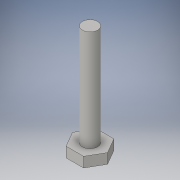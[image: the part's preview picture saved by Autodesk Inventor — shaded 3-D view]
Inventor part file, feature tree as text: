
AUTODESK INVENTOR PART (.ipt)
format: ipt  version: 2016 (Build 200138000, 138)  size: 100,864 bytes
history: native  units: in
note: dims shown in document units (in); Inventor stores cm internally (conversion verified against a paired STEP export)
features: sketch x3, extrude x2
ambient origin geometry x8: Origin, YZ Plane, XZ Plane, XY Plane, X Axis, Y Axis, Z Axis, Center Point
bodies: Solid1 (feature_tree)
feature tree (5):
  extrude  "Extrusion1"  Depth=0.25in TaperAngle=0.0deg
  extrude  "Extrusion2"  Depth=2.5in TaperAngle=0.0deg
  sketch  "Sketch3"
  sketch  "Sketch1"  dims[d0=0.375in d1=0.25in d2=0.0in]
  sketch  "Sketch2"  dims[d3=0.375in d4=2.5in d5=0.0in]
